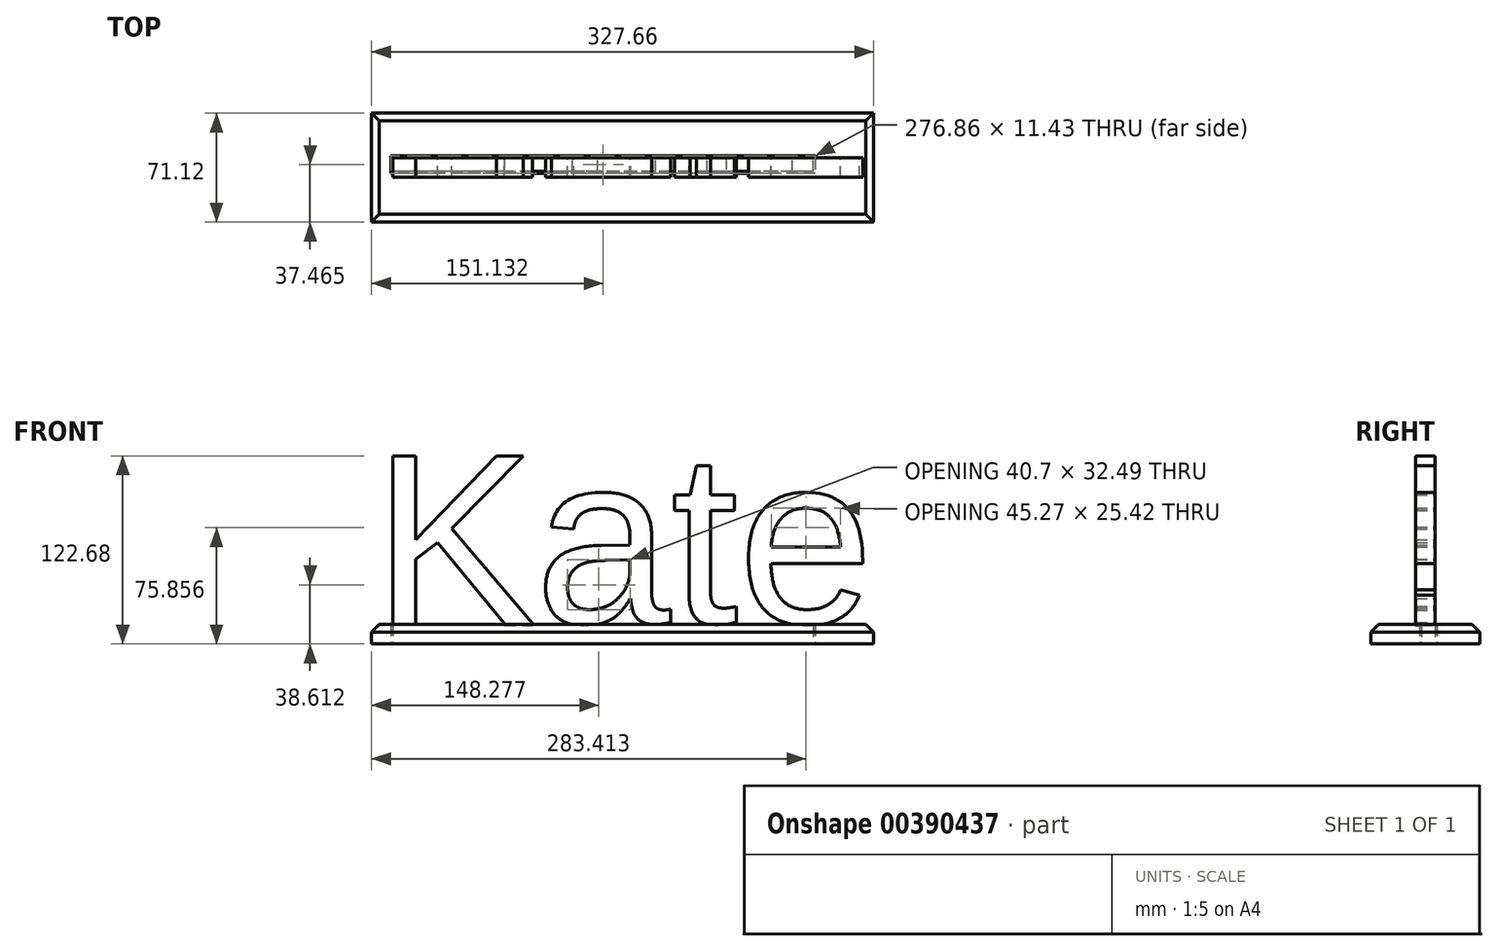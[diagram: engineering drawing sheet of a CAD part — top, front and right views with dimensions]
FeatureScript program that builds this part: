
annotation { "Feature Type Name" : "Feature", "Feature Type Description" : "" }
export const myFeature = defineFeature(function(context is Context, id is Id, definition is map)
    precondition{}
    {
        {
            var Q0;
            Q0=qCreatedBy(makeId("Front.planeOp"),FACE);
            var sketch = newSketch(context, id + "F0", { "sketchPlane" : qUnion([Q0])});
            skText(sketch, "E0", { "text": "Kate", "fontName": "Arimo-Regular.ttf"});
            const initialGuessF0  = {"E0": [0, 0, 1, 0, 0.1143]};
            skSetInitialGuess(sketch, initialGuessF0);
            skSolve(sketch);
        }
        {
            var Q0;
            Q0 = qSketchRegion(id + "F0", true);
            extrude(context, id + "F1", {"entities" : qUnion([Q0]), "depth" : 12.7 * mm});
        }
        {
            var Q0;
            Q0=makeQuery(id+"F1.opExtrude","SWEPT_FACE",FACE,{"disambiguationData":[OSD([sQuery(id+"F0.wireOp",EDGE,"E0.sketch_text.stroke-3")])]});
            var sketch = newSketch(context, id + "F2", { "sketchPlane" : qUnion([Q0])});
            skLineSegment(sketch, "E1.bottom", {"start": v(13.02, 12.7) * mm, "end": v(27.83, 12.7) * mm});
            skLineSegment(sketch, "E1.top", {"start": v(13.02, 0) * mm, "end": v(27.83, 0) * mm});
            skLineSegment(sketch, "E1.left", {"start": v(13.02, 12.7) * mm, "end": v(13.02, 0) * mm});
            skLineSegment(sketch, "E1.right", {"start": v(27.83, 12.7) * mm, "end": v(27.83, 0) * mm});
            skSolve(sketch);
        }
        {
            var Q0;
            Q0 = qSketchRegion(id + "F2", true);
            extrude(context, id + "F3", {"entities" : qUnion([Q0]), "operationType" : NewBodyOperationType.ADD, "depth" : 0.76 * mm});
        }
        {
            var Q0;
            Q0=makeQuery(id+"F1.opExtrude","SWEPT_FACE",FACE,{"disambiguationData":[OSD([sQuery(id+"F0.wireOp",EDGE,"E0.sketch_text.stroke-11")])]});
            var sketch = newSketch(context, id + "F4", { "sketchPlane" : qUnion([Q0])});
            skLineSegment(sketch, "E2.bottom", {"start": v(85.73, 12.7) * mm, "end": v(104.1, 12.7) * mm});
            skLineSegment(sketch, "E2.top", {"start": v(85.73, 0) * mm, "end": v(104.1, 0) * mm});
            skLineSegment(sketch, "E2.left", {"start": v(85.73, 12.7) * mm, "end": v(85.73, 0) * mm});
            skLineSegment(sketch, "E2.right", {"start": v(104.1, 12.7) * mm, "end": v(104.1, 0) * mm});
            skSolve(sketch);
        }
        {
            var Q0;
            Q0 = qSketchRegion(id + "F4", true);
            extrude(context, id + "F5", {"entities" : qUnion([Q0]), "operationType" : NewBodyOperationType.ADD, "depth" : 1.27 * mm});
        }
        {
            var Q0;
            Q0=makeQuery(id+"F3.boolean.opBoolean","MERGE",FACE,{"derivedFrom":[makeQuery(id+"F1.opExtrude","SWEPT_FACE",FACE,{"disambiguationData":[OSD([sQuery(id+"F0.wireOp",EDGE,"E0.sketch_text.stroke-4")])]}),makeQuery(id+"F3.opExtrude","SWEPT_FACE",FACE,{"disambiguationData":[OSD([sQuery(id+"F2.wireOp",EDGE,"E1.left")])]})]});
            var sketch = newSketch(context, id + "F6", { "sketchPlane" : qUnion([Q0])});
            skLineSegment(sketch, "E3.bottom", {"start": v(0, -0.76) * mm, "end": v(8.9, -0.76) * mm});
            skLineSegment(sketch, "E3.top", {"start": v(0, -13.46) * mm, "end": v(8.9, -13.46) * mm});
            skLineSegment(sketch, "E3.left", {"start": v(0, -0.76) * mm, "end": v(0, -13.46) * mm});
            skLineSegment(sketch, "E3.right", {"start": v(8.9, -0.76) * mm, "end": v(8.9, -13.46) * mm});
            skSolve(sketch);
        }
        {
            var Q0;
            Q0 = qSketchRegion(id + "F6", true);
            extrude(context, id + "F7", {"entities" : qUnion([Q0]), "operationType" : NewBodyOperationType.ADD, "oppositeDirection" : true, "depth" : 274.32 * mm});
        }
        {
            var Q0;
            Q0=makeQuery(id+"F7.opExtrude","SWEPT_FACE",FACE,{"disambiguationData":[OSD([sQuery(id+"F6.wireOp",EDGE,"E3.top")])]});
            var sketch = newSketch(context, id + "F8", { "sketchPlane" : qUnion([Q0])});
            skLineSegment(sketch, "E4.0", {"start": v(11.75, 10.16) * mm, "end": v(11.75, -1.27) * mm});
            skLineSegment(sketch, "E4.1", {"start": v(288.61, 10.16) * mm, "end": v(11.75, 10.16) * mm});
            skLineSegment(sketch, "E4.2", {"start": v(288.61, -1.27) * mm, "end": v(288.61, 10.16) * mm});
            skLineSegment(sketch, "E4.3", {"start": v(11.75, -1.27) * mm, "end": v(288.61, -1.27) * mm});
            skLineSegment(sketch, "E5.bottom", {"start": v(-0.95, 41.9) * mm, "end": v(326.71, 41.9) * mm});
            skLineSegment(sketch, "E5.top", {"start": v(-0.95, -29.21) * mm, "end": v(326.71, -29.2) * mm});
            skLineSegment(sketch, "E5.left", {"start": v(-0.95, 41.9) * mm, "end": v(-0.95, -29.21) * mm});
            skLineSegment(sketch, "E5.right", {"start": v(326.71, 41.9) * mm, "end": v(326.71, -29.2) * mm});
            skSolve(sketch);
        }
        {
            var Q0;
            Q0 = qSketchRegion(id + "F8", true);
            extrude(context, id + "F9", {"entities" : qUnion([Q0]), "oppositeDirection" : true, "depth" : 12.7 * mm});
        }
        {
            var Q0;
            Q0=makeQuery(id+"F9.opExtrude","CAP_EDGE",EDGE,{"disambiguationData":[OSD([sQuery(id+"F8.wireOp",EDGE,"E5.bottom")])],"isStart":false});
            var Q1;
            Q1=makeQuery(id+"F9.opExtrude","CAP_EDGE",EDGE,{"disambiguationData":[OSD([sQuery(id+"F8.wireOp",EDGE,"E5.right")])],"isStart":false});
            var Q2;
            Q2=makeQuery(id+"F9.opExtrude","CAP_EDGE",EDGE,{"disambiguationData":[OSD([sQuery(id+"F8.wireOp",EDGE,"E5.top")])],"isStart":false});
            var Q3;
            Q3=makeQuery(id+"F9.opExtrude","CAP_EDGE",EDGE,{"disambiguationData":[OSD([sQuery(id+"F8.wireOp",EDGE,"E5.left")])],"isStart":false});
            chamfer(context, id + "F10", {"entities" : qUnion([Q0, Q1, Q2, Q3]), "width" : 5.08 * mm, "tangentPropagation" : true});
        }
    });
